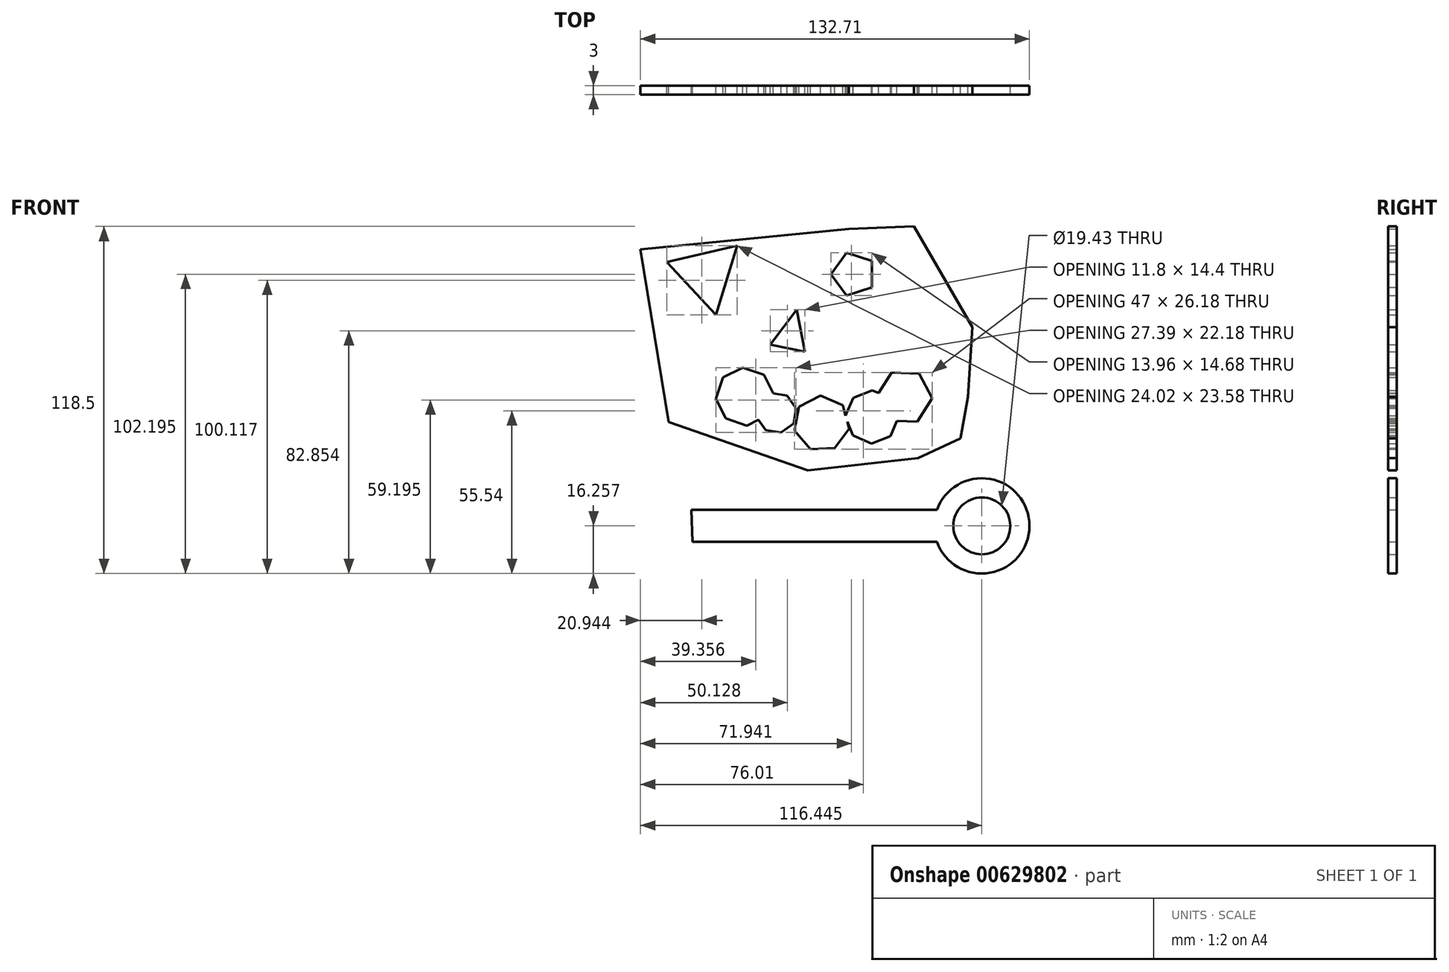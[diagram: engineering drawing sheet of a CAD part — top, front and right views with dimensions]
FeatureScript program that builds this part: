
annotation { "Feature Type Name" : "Feature", "Feature Type Description" : "" }
export const myFeature = defineFeature(function(context is Context, id is Id, definition is map)
    precondition{}
    {
        {
            var Q0;
            Q0=qCreatedBy(makeId("Front.planeOp"),FACE);
            var sketch = newSketch(context, id + "F0", { "sketchPlane" : qUnion([Q0])});
            skCircle(sketch, "E0.cCircle", {"center": v(-39.2, 34.6) * mm, "radius": 7.12 * mm, "construction": true});
            skLineSegment(sketch, "E0.0", {"start": v(-36, 20.73) * mm, "end": v(-52.82, 38.76) * mm});
            skLineSegment(sketch, "E0.1", {"start": v(-52.82, 38.76) * mm, "end": v(-28.8, 44.32) * mm});
            skLineSegment(sketch, "E0.2", {"start": v(-28.8, 44.32) * mm, "end": v(-36, 20.73) * mm});
            skPoint(sketch, "E0.0.midPoint", {"position": v(-44.4, 29.75) * mm});
            skCircle(sketch, "E1.cCircle", {"center": v(10.93, 34.6) * mm, "radius": 6.24 * mm, "construction": true});
            skLineSegment(sketch, "E1.0", {"start": v(17.17, 39.14) * mm, "end": v(17.17, 30.07) * mm});
            skLineSegment(sketch, "E1.1", {"start": v(17.17, 30.07) * mm, "end": v(8.54, 27.26) * mm});
            skLineSegment(sketch, "E1.2", {"start": v(8.54, 27.26) * mm, "end": v(3.2, 34.6) * mm});
            skLineSegment(sketch, "E1.3", {"start": v(3.2, 34.6) * mm, "end": v(8.54, 41.95) * mm});
            skLineSegment(sketch, "E1.4", {"start": v(8.54, 41.95) * mm, "end": v(17.17, 39.14) * mm});
            skPoint(sketch, "E1.0.midPoint", {"position": v(17.17, 34.6) * mm});
            skCircle(sketch, "E2.cCircle", {"center": v(-26.2, -7.2) * mm, "radius": 9.16 * mm, "construction": true});
            skLineSegment(sketch, "E2.0", {"start": v(-16.3, -6.55) * mm, "end": v(-18.74, -13.74) * mm});
            skLineSegment(sketch, "E2.1", {"start": v(-18.74, -13.74) * mm, "end": v(-25.55, -17.1) * mm});
            skLineSegment(sketch, "E2.2", {"start": v(-25.55, -17.1) * mm, "end": v(-32.73, -14.65) * mm});
            skLineSegment(sketch, "E2.3", {"start": v(-32.73, -14.65) * mm, "end": v(-36.09, -7.84) * mm});
            skLineSegment(sketch, "E2.4", {"start": v(-36.09, -7.84) * mm, "end": v(-33.64, -0.66) * mm});
            skLineSegment(sketch, "E2.5", {"start": v(-33.64, -0.66) * mm, "end": v(-26.84, 2.7) * mm});
            skLineSegment(sketch, "E2.6", {"start": v(-26.84, 2.7) * mm, "end": v(-19.65, 0.25) * mm});
            skLineSegment(sketch, "E2.7", {"start": v(-19.65, 0.25) * mm, "end": v(-16.3, -6.55) * mm});
            skPoint(sketch, "E2.0.midPoint", {"position": v(-17.52, -10.15) * mm});
            skCircle(sketch, "E3.cCircle", {"center": v(-15.44, -12.75) * mm, "radius": 6.4 * mm, "construction": true});
            skLineSegment(sketch, "E3.0", {"start": v(-9.53, -16.37) * mm, "end": v(-13.82, -19.49) * mm});
            skLineSegment(sketch, "E3.1", {"start": v(-13.82, -19.49) * mm, "end": v(-19.06, -18.66) * mm});
            skLineSegment(sketch, "E3.2", {"start": v(-19.06, -18.66) * mm, "end": v(-22.18, -14.37) * mm});
            skLineSegment(sketch, "E3.3", {"start": v(-22.18, -14.37) * mm, "end": v(-21.35, -9.13) * mm});
            skLineSegment(sketch, "E3.4", {"start": v(-21.35, -9.13) * mm, "end": v(-17.06, -6.01) * mm});
            skLineSegment(sketch, "E3.5", {"start": v(-17.06, -6.01) * mm, "end": v(-11.82, -6.84) * mm});
            skLineSegment(sketch, "E3.6", {"start": v(-11.82, -6.84) * mm, "end": v(-8.7, -11.13) * mm});
            skLineSegment(sketch, "E3.7", {"start": v(-8.7, -11.13) * mm, "end": v(-9.53, -16.37) * mm});
            skPoint(sketch, "E3.0.midPoint", {"position": v(-11.68, -17.93) * mm});
            skCircle(sketch, "E4.cCircle", {"center": v(0, -16.37) * mm, "radius": 8.62 * mm, "construction": true});
            skLineSegment(sketch, "E4.0", {"start": v(7.25, -10.13) * mm, "end": v(9.4, -18.15) * mm});
            skLineSegment(sketch, "E4.1", {"start": v(9.4, -18.15) * mm, "end": v(4.47, -24.83) * mm});
            skLineSegment(sketch, "E4.2", {"start": v(4.47, -24.83) * mm, "end": v(-3.82, -25.14) * mm});
            skLineSegment(sketch, "E4.3", {"start": v(-3.82, -25.14) * mm, "end": v(-9.24, -18.85) * mm});
            skLineSegment(sketch, "E4.4", {"start": v(-9.24, -18.85) * mm, "end": v(-7.7, -10.69) * mm});
            skLineSegment(sketch, "E4.5", {"start": v(-7.7, -10.69) * mm, "end": v(-0.36, -6.8) * mm});
            skLineSegment(sketch, "E4.6", {"start": v(-0.36, -6.8) * mm, "end": v(7.25, -10.13) * mm});
            skPoint(sketch, "E4.0.midPoint", {"position": v(8.33, -14.14) * mm});
            skCircle(sketch, "E5.cCircle", {"center": v(17.17, -14.14) * mm, "radius": 8.4 * mm, "construction": true});
            skLineSegment(sketch, "E5.0", {"start": v(23.68, -7.78) * mm, "end": v(26.27, -14.25) * mm});
            skLineSegment(sketch, "E5.1", {"start": v(26.27, -14.25) * mm, "end": v(23.53, -20.65) * mm});
            skLineSegment(sketch, "E5.2", {"start": v(23.53, -20.65) * mm, "end": v(17.06, -23.24) * mm});
            skLineSegment(sketch, "E5.3", {"start": v(17.06, -23.24) * mm, "end": v(10.66, -20.5) * mm});
            skLineSegment(sketch, "E5.4", {"start": v(10.66, -20.5) * mm, "end": v(8.07, -14.03) * mm});
            skLineSegment(sketch, "E5.5", {"start": v(8.07, -14.03) * mm, "end": v(10.82, -7.62) * mm});
            skLineSegment(sketch, "E5.6", {"start": v(10.82, -7.62) * mm, "end": v(17.28, -5.04) * mm});
            skLineSegment(sketch, "E5.7", {"start": v(17.28, -5.04) * mm, "end": v(23.68, -7.78) * mm});
            skPoint(sketch, "E5.0.midPoint", {"position": v(24.98, -11.01) * mm});
            skCircle(sketch, "E6.cCircle", {"center": v(28.27, -7.37) * mm, "radius": 8.22 * mm, "construction": true});
            skLineSegment(sketch, "E6.0", {"start": v(33.36, 0.65) * mm, "end": v(37.76, -7.76) * mm});
            skLineSegment(sketch, "E6.1", {"start": v(37.76, -7.76) * mm, "end": v(32.68, -15.78) * mm});
            skLineSegment(sketch, "E6.2", {"start": v(32.68, -15.78) * mm, "end": v(23.2, -15.4) * mm});
            skLineSegment(sketch, "E6.3", {"start": v(23.2, -15.4) * mm, "end": v(18.79, -6.98) * mm});
            skLineSegment(sketch, "E6.4", {"start": v(18.79, -6.98) * mm, "end": v(23.87, 1.04) * mm});
            skLineSegment(sketch, "E6.5", {"start": v(23.87, 1.04) * mm, "end": v(33.36, 0.65) * mm});
            skPoint(sketch, "E6.0.midPoint", {"position": v(35.56, -3.56) * mm});
            skLineSegment(sketch, "E7", {"start": v(-61.75, 43.1) * mm, "end": v(-52.21, -15.87) * mm});
            skLineSegment(sketch, "E8", {"start": v(-52.21, -15.87) * mm, "end": v(-4.68, -32.35) * mm});
            skLineSegment(sketch, "E9", {"start": v(-4.68, -32.35) * mm, "end": v(32.96, -28.19) * mm});
            skLineSegment(sketch, "E10", {"start": v(32.96, -28.19) * mm, "end": v(47.35, -21.42) * mm});
            skLineSegment(sketch, "E11", {"start": v(47.35, -21.42) * mm, "end": v(49.96, -7.37) * mm});
            skLineSegment(sketch, "E12", {"start": v(49.96, -7.37) * mm, "end": v(51.52, 16.57) * mm});
            skLineSegment(sketch, "E13", {"start": v(51.52, 16.57) * mm, "end": v(31.57, 50.9) * mm});
            skLineSegment(sketch, "E14", {"start": v(31.57, 50.9) * mm, "end": v(9.36, 50.07) * mm});
            skLineSegment(sketch, "E15", {"start": v(9.36, 50.07) * mm, "end": v(-61.75, 43.1) * mm});
            skLineSegment(sketch, "E16", {"start": v(-17.52, 10.5) * mm, "end": v(-5.72, 8.07) * mm});
            skLineSegment(sketch, "E17", {"start": v(-5.72, 8.07) * mm, "end": v(-8.5, 22.46) * mm});
            skLineSegment(sketch, "E18", {"start": v(-8.5, 22.46) * mm, "end": v(-17.52, 10.5) * mm});
            skLineSegment(sketch, "E19", {"start": v(-44.4, -45.88) * mm, "end": v(39.37, -45.88) * mm});
            skLineSegment(sketch, "E20", {"start": v(-44.4, -45.88) * mm, "end": v(-44, -56.79) * mm});
            skLineSegment(sketch, "E21", {"start": v(-44, -56.79) * mm, "end": v(39.37, -56.79) * mm});
            skArc(sketch, "E22", {"start": v(39.37, -56.79) * mm, "mid": v(70.96, -51.33) * mm, "end": v(39.37, -45.88) * mm});
            skCircle(sketch, "E23", {"center": v(54.7, -51.33) * mm, "radius": 9.71 * mm});
            skSolve(sketch);
        }
        {
            var Q0;
            Q0=makeQuery(id+"F0.imprint","IMPRINT",FACE,{"disambiguationData":[TD([[makeQuery(id+"F0.imprint","IMPRINT",EDGE,{"derivedFrom":sQuery(id+"F0.wireOp",EDGE,"E0.0")}),1.0]])]});
            var Q1;
            Q1=makeQuery(id+"F0.imprint","IMPRINT",FACE,{"disambiguationData":[TD([[makeQuery(id+"F0.imprint","IMPRINT",EDGE,{"derivedFrom":sQuery(id+"F0.wireOp",EDGE,"E19")}),-1.0]])]});
            extrude(context, id + "F1", {"entities" : qUnion([Q0, Q1]), "depth" : 3 * mm, "offsetDistance" : 25 * mm});
        }
    });
